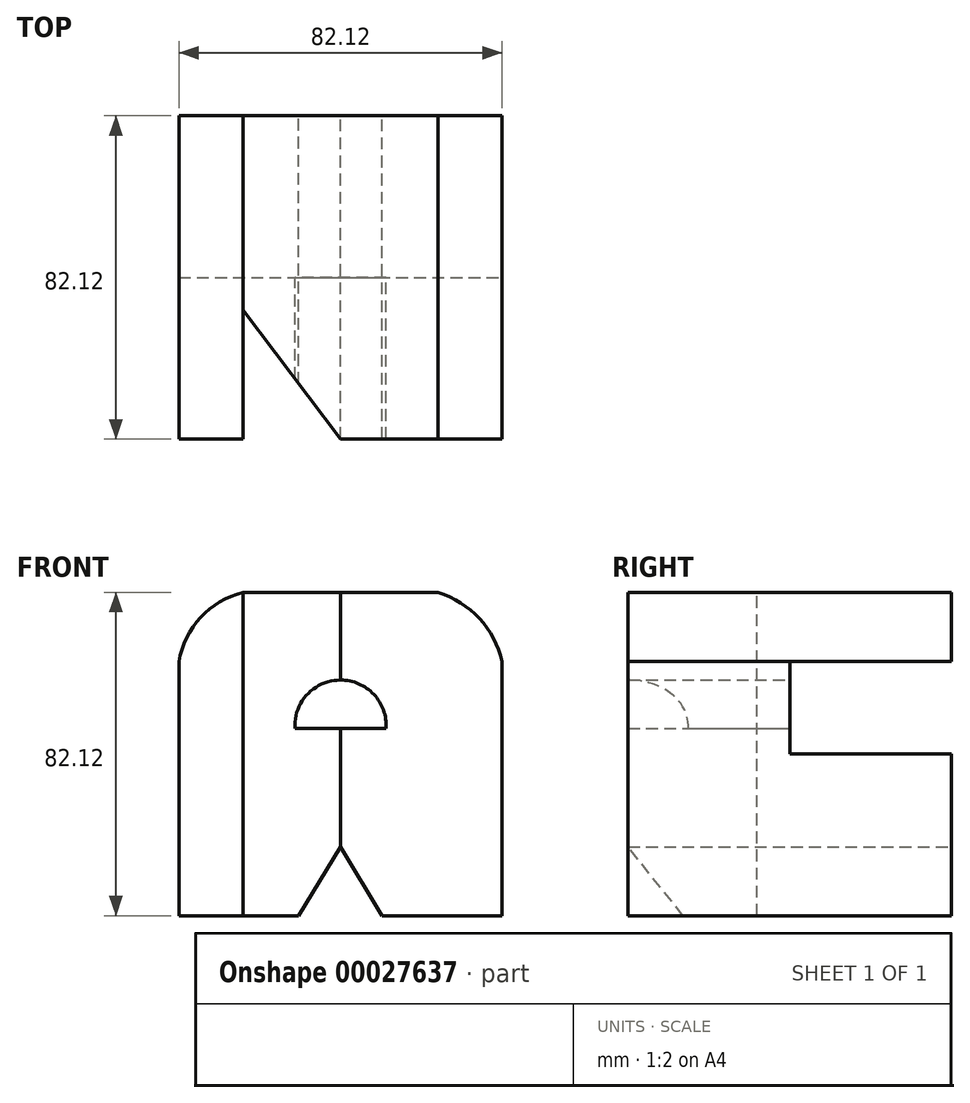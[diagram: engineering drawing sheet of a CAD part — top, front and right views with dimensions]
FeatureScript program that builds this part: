
annotation { "Feature Type Name" : "Feature", "Feature Type Description" : "" }
export const myFeature = defineFeature(function(context is Context, id is Id, definition is map)
    precondition{}
    {
        {
            var Q0;
            Q0=qCreatedBy(makeId("Front.planeOp"),FACE);
            var sketch = newSketch(context, id + "F0", { "sketchPlane" : qUnion([Q0])});
            skLineSegment(sketch, "E0.rect.bottom", {"start": v(-41.06, 41.06) * mm, "end": v(41.06, 41.06) * mm});
            skLineSegment(sketch, "E0.rect.top", {"start": v(-41.06, -41.06) * mm, "end": v(41.06, -41.06) * mm});
            skLineSegment(sketch, "E0.rect.left", {"start": v(-41.06, 41.06) * mm, "end": v(-41.06, -41.06) * mm});
            skLineSegment(sketch, "E0.rect.right", {"start": v(41.06, 41.06) * mm, "end": v(41.06, -41.06) * mm});
            skPoint(sketch, "E0.rect.middle", {"position": v(0, 0) * mm});
            skSolve(sketch);
        }
        {
            var Q0;
            Q0=makeQuery(id+"F0.imprint","IMPRINT",FACE,{"disambiguationData":[TD([[makeQuery(id+"F0.imprint","IMPRINT",EDGE,{"derivedFrom":sQuery(id+"F0.wireOp",EDGE,"E0.rect.bottom")}),-1.0]])]});
            extrude(context, id + "F1", {"entities" : qUnion([Q0]), "endBound" : BoundingType.SYMMETRIC, "depth" : 82.13 * mm});
        }
        {
            var Q0;
            Q0=makeQuery(id+"F1.opExtrude","CAP_FACE",FACE,{"disambiguationData":[OSD([sQuery(id+"F0.wireOp",EDGE,"E0.rect.bottom"),sQuery(id+"F0.wireOp",EDGE,"E0.rect.top"),sQuery(id+"F0.wireOp",EDGE,"E0.rect.left"),sQuery(id+"F0.wireOp",EDGE,"E0.rect.right")])],"isStart":true});
            var sketch = newSketch(context, id + "F2", { "sketchPlane" : qUnion([Q0])});
            skArc(sketch, "E1", {"start": v(-24.8, 41.06) * mm, "mid": v(-35.29, 34.47) * mm, "end": v(-41.06, 23.52) * mm});
            skArc(sketch, "E2", {"start": v(41.06, 23.52) * mm, "mid": v(35.54, 34.7) * mm, "end": v(24.8, 41.06) * mm});
            skLineSegment(sketch, "E3", {"start": v(-41.06, 23.52) * mm, "end": v(-41.06, 41.06) * mm});
            skLineSegment(sketch, "E4", {"start": v(-41.06, 41.06) * mm, "end": v(-24.8, 41.06) * mm});
            skLineSegment(sketch, "E5", {"start": v(24.8, 41.06) * mm, "end": v(41.06, 41.06) * mm});
            skLineSegment(sketch, "E6", {"start": v(41.06, 41.06) * mm, "end": v(41.06, 23.52) * mm});
            skLineSegment(sketch, "E7", {"start": v(0, 6.5) * mm, "end": v(11.6, 6.5) * mm});
            skLineSegment(sketch, "E8", {"start": v(0, 6.5) * mm, "end": v(-11.6, 6.5) * mm});
            skArc(sketch, "E9", {"start": v(11.6, 6.5) * mm, "mid": v(0, 18.82) * mm, "end": v(-11.6, 6.5) * mm});
            skLineSegment(sketch, "E10", {"start": v(0, -23.56) * mm, "end": v(-10.6, -41.06) * mm});
            skLineSegment(sketch, "E11", {"start": v(0, -23.56) * mm, "end": v(10.6, -41.06) * mm});
            skLineSegment(sketch, "E12", {"start": v(10.6, -41.06) * mm, "end": v(0, -41.06) * mm});
            skLineSegment(sketch, "E13", {"start": v(0, -41.06) * mm, "end": v(-10.6, -41.06) * mm});
            skSolve(sketch);
        }
        {
            var Q0;
            Q0=makeQuery(id+"F2.imprint","IMPRINT",FACE,{"disambiguationData":[TD([[makeQuery(id+"F2.imprint","IMPRINT",EDGE,{"derivedFrom":sQuery(id+"F2.wireOp",EDGE,"E10")}),1.0]])]});
            var Q1;
            Q1=makeQuery(id+"F2.imprint","IMPRINT",FACE,{"disambiguationData":[TD([[makeQuery(id+"F2.imprint","IMPRINT",EDGE,{"derivedFrom":sQuery(id+"F2.wireOp",EDGE,"E7")}),1.0]])]});
            var Q2;
            Q2=makeQuery(id+"F2.imprint","IMPRINT",FACE,{"disambiguationData":[TD([[makeQuery(id+"F2.imprint","IMPRINT",EDGE,{"derivedFrom":sQuery(id+"F2.wireOp",EDGE,"E1")}),-1.0]])]});
            var Q3;
            Q3=makeQuery(id+"F2.imprint","IMPRINT",FACE,{"disambiguationData":[TD([[makeQuery(id+"F2.imprint","IMPRINT",EDGE,{"derivedFrom":sQuery(id+"F2.wireOp",EDGE,"E2")}),-1.0]])]});
            extrude(context, id + "F3", {"entities" : qUnion([Q0, Q1, Q2, Q3]), "operationType" : NewBodyOperationType.REMOVE, "endBound" : BoundingType.THROUGH_ALL, "oppositeDirection" : true, "depth" : 25 * mm});
        }
        {
            var Q0;
            Q0=makeQuery(id+"F1.opExtrude","SWEPT_FACE",FACE,{"disambiguationData":[OSD([sQuery(id+"F0.wireOp",EDGE,"E0.rect.right")])]});
            var sketch = newSketch(context, id + "F4", { "sketchPlane" : qUnion([Q0])});
            skLineSegment(sketch, "E14.0.0", {"start": v(-41.06, 23.52) * mm, "end": v(41.06, 23.52) * mm});
            skLineSegment(sketch, "E14.0.1", {"start": v(41.06, 23.52) * mm, "end": v(41.06, 41.06) * mm});
            skLineSegment(sketch, "E14.0.2", {"start": v(41.06, 41.06) * mm, "end": v(-41.06, 41.06) * mm});
            skLineSegment(sketch, "E14.0.3", {"start": v(-41.06, 41.06) * mm, "end": v(-41.06, 23.52) * mm});
            skLineSegment(sketch, "E15.bottom", {"start": v(0, 41.06) * mm, "end": v(41.06, 41.06) * mm});
            skLineSegment(sketch, "E15.top", {"start": v(0, 0) * mm, "end": v(41.06, 0) * mm});
            skLineSegment(sketch, "E15.left", {"start": v(0, 41.06) * mm, "end": v(0, 0) * mm});
            skLineSegment(sketch, "E15.right", {"start": v(41.06, 41.06) * mm, "end": v(41.06, 0) * mm});
            skSolve(sketch);
        }
        {
            var Q0;
            {var subQ1=sQuery(id+"F4.wireOp",EDGE,"E15.top");Q0=makeQuery(id+"F4.imprint","IMPRINT",FACE,{"disambiguationData":[TD([[makeQuery(id+"F4.imprint","IMPRINT",EDGE,{"derivedFrom":subQ1}),1.0]])]});}
            var Q1;
            {var subQ1=sQuery(id+"F4.wireOp",EDGE,"E15.bottom");Q1=makeQuery(id+"F4.imprint","IMPRINT",FACE,{"disambiguationData":[TD([[makeQuery(id+"F4.imprint","IMPRINT",EDGE,{"derivedFrom":subQ1}),-1.0]])]});}
            extrude(context, id + "F5", {"entities" : qUnion([Q0, Q1]), "operationType" : NewBodyOperationType.REMOVE, "endBound" : BoundingType.THROUGH_ALL, "oppositeDirection" : true, "depth" : 25 * mm});
        }
        {
            var Q0;
            Q0=makeQuery(id+"F1.opExtrude","SWEPT_FACE",FACE,{"disambiguationData":[OSD([sQuery(id+"F0.wireOp",EDGE,"E0.rect.bottom")])]});
            var sketch = newSketch(context, id + "F6", { "sketchPlane" : qUnion([Q0])});
            skLineSegment(sketch, "E16.0.0", {"start": v(-41.06, 0) * mm, "end": v(-24.8, 0) * mm});
            skLineSegment(sketch, "E16.0.1", {"start": v(-41.06, 0) * mm, "end": v(-41.06, -41.06) * mm});
            skLineSegment(sketch, "E16.0.2", {"start": v(-41.06, -41.06) * mm, "end": v(-24.8, -41.06) * mm});
            skLineSegment(sketch, "E16.0.3", {"start": v(-24.8, -41.06) * mm, "end": v(-24.8, 0) * mm});
            skLineSegment(sketch, "E16.1.0", {"start": v(24.8, 0) * mm, "end": v(41.06, 0) * mm});
            skLineSegment(sketch, "E16.1.1", {"start": v(24.8, 0) * mm, "end": v(24.8, -41.06) * mm});
            skLineSegment(sketch, "E16.1.2", {"start": v(24.8, -41.06) * mm, "end": v(41.06, -41.06) * mm});
            skLineSegment(sketch, "E16.1.3", {"start": v(41.06, -41.06) * mm, "end": v(41.06, 0) * mm});
            skLineSegment(sketch, "E16.2.0", {"start": v(-41.06, 0) * mm, "end": v(41.06, 0) * mm});
            skLineSegment(sketch, "E16.2.1", {"start": v(41.06, 0) * mm, "end": v(41.06, 41.06) * mm});
            skLineSegment(sketch, "E16.2.2", {"start": v(41.06, 41.06) * mm, "end": v(-41.06, 41.06) * mm});
            skLineSegment(sketch, "E16.2.3", {"start": v(-41.06, 41.06) * mm, "end": v(-41.06, 0) * mm});
            skLineSegment(sketch, "E17", {"start": v(0, -41.06) * mm, "end": v(-24.8, -8.33) * mm});
            skLineSegment(sketch, "E18", {"start": v(-24.8, -8.33) * mm, "end": v(-24.8, -41.06) * mm});
            skLineSegment(sketch, "E19", {"start": v(24.8, 41.06) * mm, "end": v(0, 41.06) * mm});
            skLineSegment(sketch, "E20", {"start": v(0, 41.06) * mm, "end": v(24.8, 8.33) * mm});
            skLineSegment(sketch, "E21", {"start": v(24.8, 8.33) * mm, "end": v(24.8, 41.06) * mm});
            skPoint(sketch, "E22", {"position": v(0, -41.06) * mm});
            skSolve(sketch);
        }
        {
            var Q0;
            Q0=makeQuery(id+"F6.imprint","IMPRINT",FACE,{"disambiguationData":[TD([[makeQuery(id+"F6.imprint","IMPRINT",EDGE,{"derivedFrom":sQuery(id+"F6.wireOp",EDGE,"E19")}),1.0]])]});
            var Q1;
            {var subQ1=sQuery(id+"F6.wireOp",EDGE,"E17");Q1=makeQuery(id+"F6.imprint","IMPRINT",FACE,{"disambiguationData":[TD([[makeQuery(id+"F6.imprint","IMPRINT",EDGE,{"derivedFrom":subQ1}),1.0]])]});}
            extrude(context, id + "F7", {"entities" : qUnion([Q0, Q1]), "operationType" : NewBodyOperationType.REMOVE, "endBound" : BoundingType.THROUGH_ALL, "oppositeDirection" : true, "depth" : 25 * mm});
        }
        {
            var Q0;
            {var subQ1=sQuery(id+"F6.wireOp",EDGE,"E17");Q0=makeQuery(id+"F6.imprint","IMPRINT",FACE,{"disambiguationData":[TD([[makeQuery(id+"F6.imprint","IMPRINT",EDGE,{"derivedFrom":subQ1}),1.0]])]});}
            var Q1;
            Q1=makeQuery(id+"F6.imprint","IMPRINT",FACE,{"disambiguationData":[TD([[makeQuery(id+"F6.imprint","IMPRINT",EDGE,{"derivedFrom":sQuery(id+"F6.wireOp",EDGE,"E19")}),1.0]])]});
            extrude(context, id + "F8", {"entities" : qUnion([Q0, Q1]), "operationType" : NewBodyOperationType.REMOVE, "endBound" : BoundingType.THROUGH_ALL, "oppositeDirection" : true, "depth" : 25 * mm});
        }
    });
